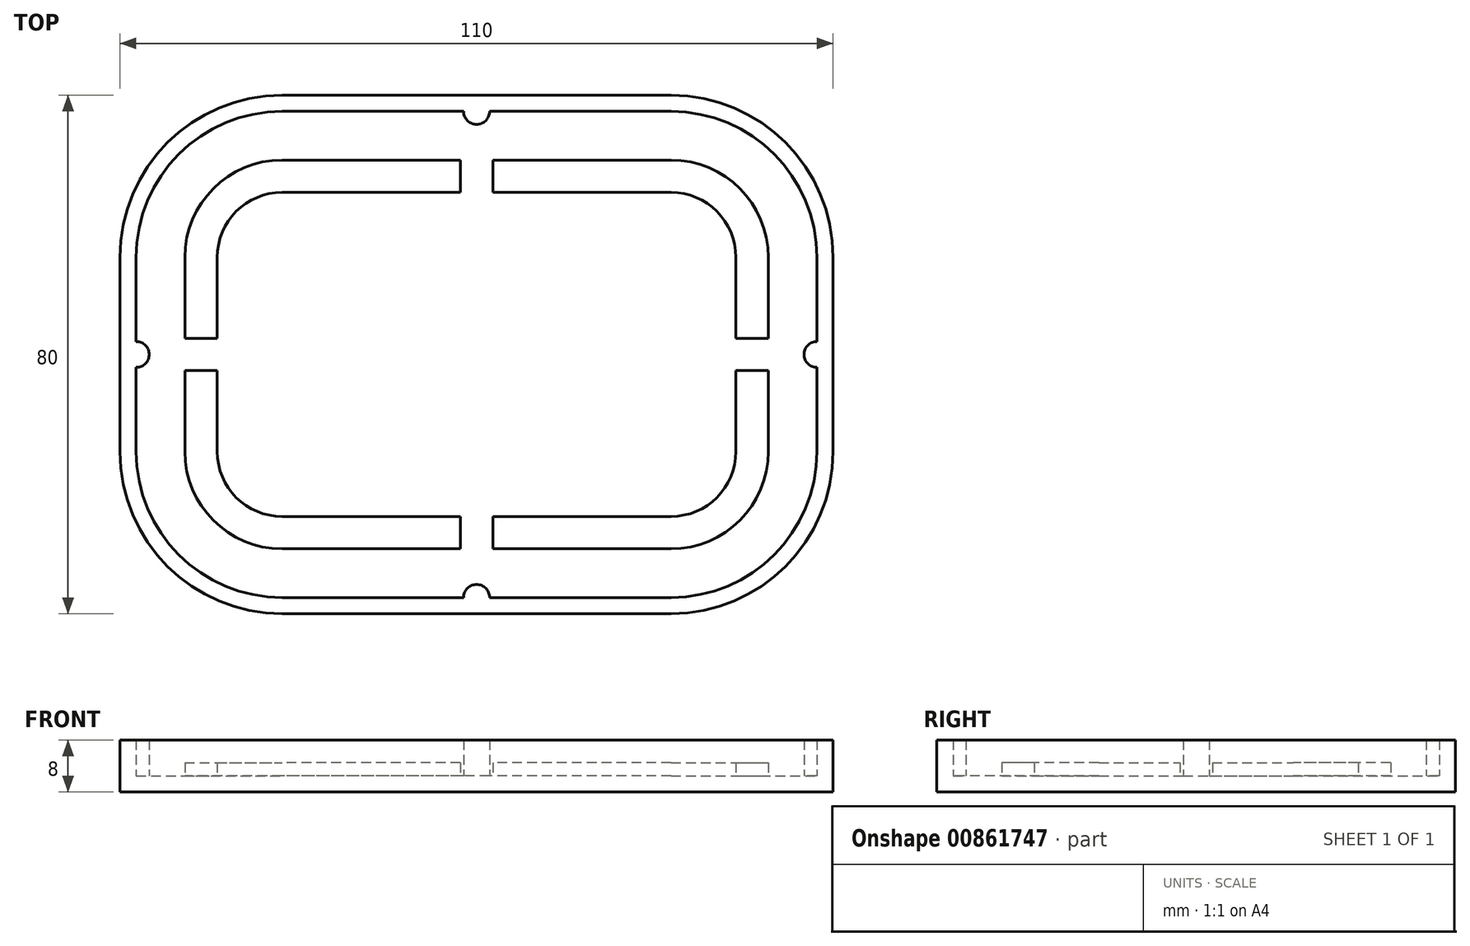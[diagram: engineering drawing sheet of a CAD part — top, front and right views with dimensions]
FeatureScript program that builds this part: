
annotation { "Feature Type Name" : "Feature", "Feature Type Description" : "" }
export const myFeature = defineFeature(function(context is Context, id is Id, definition is map)
    precondition{}
    {
        {
            var Q0;
            Q0=qCreatedBy(makeId("Top.planeOp"),FACE);
            var sketch = newSketch(context, id + "F0", { "sketchPlane" : qUnion([Q0])});
            skLineSegment(sketch, "E0.bottom", {"start": v(30, -40) * mm, "end": v(-30, -40) * mm});
            skLineSegment(sketch, "E0.top", {"start": v(30, 40) * mm, "end": v(-30, 40) * mm});
            skLineSegment(sketch, "E0.left", {"start": v(55, -15) * mm, "end": v(55, 15) * mm});
            skLineSegment(sketch, "E0.right", {"start": v(-55, -15) * mm, "end": v(-55, 15) * mm});
            skPoint(sketch, "E0.middle", {"position": v(0, 0) * mm});
            skPoint(sketch, "E1.visualSharp", {"position": v(-55, 40) * mm});
            skArc(sketch, "E1.filletArc", {"start": v(-30, 40) * mm, "mid": v(-47.68, 32.68) * mm, "end": v(-55, 15) * mm});
            skPoint(sketch, "E2.visualSharp", {"position": v(55, 40) * mm});
            skArc(sketch, "E2.filletArc", {"start": v(55, 15) * mm, "mid": v(47.68, 32.68) * mm, "end": v(30, 40) * mm});
            skPoint(sketch, "E3.visualSharp", {"position": v(55, -40) * mm});
            skArc(sketch, "E3.filletArc", {"start": v(30, -40) * mm, "mid": v(47.68, -32.68) * mm, "end": v(55, -15) * mm});
            skPoint(sketch, "E4.visualSharp", {"position": v(-55, -40) * mm});
            skArc(sketch, "E4.filletArc", {"start": v(-55, -15) * mm, "mid": v(-47.68, -32.68) * mm, "end": v(-30, -40) * mm});
            skSolve(sketch);
        }
        {
            var Q0;
            Q0=makeQuery(id+"F0.imprint","IMPRINT",FACE,{"disambiguationData":[TD([[makeQuery(id+"F0.imprint","IMPRINT",EDGE,{"derivedFrom":sQuery(id+"F0.wireOp",EDGE,"E0.bottom")}),-1.0]])]});
            extrude(context, id + "F1", {"entities" : qUnion([Q0]), "depth" : 8 * mm, "offsetDistance" : 25 * mm});
        }
        {
            var Q0;
            Q0=makeQuery(id+"F1.opExtrude","CAP_FACE",FACE,{"disambiguationData":[OSD([sQuery(id+"F0.wireOp",EDGE,"E0.bottom"),sQuery(id+"F0.wireOp",EDGE,"E0.top"),sQuery(id+"F0.wireOp",EDGE,"E0.left"),sQuery(id+"F0.wireOp",EDGE,"E0.right"),sQuery(id+"F0.wireOp",EDGE,"E1.filletArc"),sQuery(id+"F0.wireOp",EDGE,"E2.filletArc"),sQuery(id+"F0.wireOp",EDGE,"E3.filletArc"),sQuery(id+"F0.wireOp",EDGE,"E4.filletArc")])],"isStart":false});
            shell(context, id + "F2", {"entities" : qUnion([Q0]), "thickness" : 2.5 * mm});
        }
        {
            var Q0;
            Q0=makeQuery(id+"F2.opShell","OFFSET_FACE",FACE,{"disambiguationData":[OSD([sQuery(id+"F0.wireOp",EDGE,"E0.bottom"),sQuery(id+"F0.wireOp",EDGE,"E0.top"),sQuery(id+"F0.wireOp",EDGE,"E0.left"),sQuery(id+"F0.wireOp",EDGE,"E0.right"),sQuery(id+"F0.wireOp",EDGE,"E1.filletArc"),sQuery(id+"F0.wireOp",EDGE,"E2.filletArc"),sQuery(id+"F0.wireOp",EDGE,"E3.filletArc"),sQuery(id+"F0.wireOp",EDGE,"E4.filletArc")])]});
            var sketch = newSketch(context, id + "F3", { "sketchPlane" : qUnion([Q0])});
            skLineSegment(sketch, "E5.bottom", {"start": v(30, -30) * mm, "end": v(-30, -30) * mm});
            skLineSegment(sketch, "E5.top", {"start": v(30, 30) * mm, "end": v(-30, 30) * mm});
            skLineSegment(sketch, "E5.left", {"start": v(45, -15) * mm, "end": v(45, 15) * mm});
            skLineSegment(sketch, "E5.right", {"start": v(-45, -15) * mm, "end": v(-45, 15) * mm});
            skPoint(sketch, "E5.middle", {"position": v(0, 0) * mm});
            skPoint(sketch, "E6.visualSharp", {"position": v(-45, 30) * mm});
            skArc(sketch, "E6.filletArc", {"start": v(-30, 30) * mm, "mid": v(-40.6, 25.6) * mm, "end": v(-45, 15) * mm});
            skPoint(sketch, "E7.visualSharp", {"position": v(45, 30) * mm});
            skArc(sketch, "E7.filletArc", {"start": v(45, 15) * mm, "mid": v(40.6, 25.6) * mm, "end": v(30, 30) * mm});
            skPoint(sketch, "E8.visualSharp", {"position": v(45, -30) * mm});
            skArc(sketch, "E8.filletArc", {"start": v(30, -30) * mm, "mid": v(40.6, -25.6) * mm, "end": v(45, -15) * mm});
            skPoint(sketch, "E9.visualSharp", {"position": v(-45, -30) * mm});
            skArc(sketch, "E9.filletArc", {"start": v(-45, -15) * mm, "mid": v(-40.6, -25.6) * mm, "end": v(-30, -30) * mm});
            skArc(sketch, "E10.0", {"start": v(40, 15) * mm, "mid": v(37.07, 22.07) * mm, "end": v(30, 25) * mm});
            skLineSegment(sketch, "E10.1", {"start": v(40, -15) * mm, "end": v(40, 15) * mm});
            skLineSegment(sketch, "E10.2", {"start": v(30, 25) * mm, "end": v(-30, 25) * mm});
            skArc(sketch, "E10.3", {"start": v(30, -25) * mm, "mid": v(37.07, -22.07) * mm, "end": v(40, -15) * mm});
            skArc(sketch, "E10.4", {"start": v(-30, 25) * mm, "mid": v(-37.07, 22.07) * mm, "end": v(-40, 15) * mm});
            skLineSegment(sketch, "E10.5", {"start": v(-40, -15) * mm, "end": v(-40, 15) * mm});
            skArc(sketch, "E10.6", {"start": v(-40, -15) * mm, "mid": v(-37.07, -22.07) * mm, "end": v(-30, -25) * mm});
            skLineSegment(sketch, "E10.7", {"start": v(30, -25) * mm, "end": v(-30, -25) * mm});
            skLineSegment(sketch, "E11", {"start": v(-2.5, 30) * mm, "end": v(-2.5, -30) * mm});
            skLineSegment(sketch, "E12", {"start": v(2.5, -30) * mm, "end": v(2.5, 30) * mm});
            skLineSegment(sketch, "E13", {"start": v(-45, 2.5) * mm, "end": v(45, 2.5) * mm});
            skLineSegment(sketch, "E14", {"start": v(-45, -2.5) * mm, "end": v(45, -2.5) * mm});
            skSolve(sketch);
        }
        {
            var Q0;
            {var subQ4=sQuery(id+"F3.wireOp",EDGE,"E6.filletArc");Q0=makeQuery(id+"F3.imprint","IMPRINT",FACE,{"disambiguationData":[TD([[makeQuery(id+"F3.imprint","IMPRINT",EDGE,{"derivedFrom":subQ4}),1.0]])]});}
            var Q1;
            {var subQ1=sQuery(id+"F3.wireOp",EDGE,"E7.filletArc");Q1=makeQuery(id+"F3.imprint","IMPRINT",FACE,{"disambiguationData":[TD([[makeQuery(id+"F3.imprint","IMPRINT",EDGE,{"derivedFrom":subQ1}),1.0]])]});}
            var Q2;
            {var subQ4=sQuery(id+"F3.wireOp",EDGE,"E8.filletArc");Q2=makeQuery(id+"F3.imprint","IMPRINT",FACE,{"disambiguationData":[TD([[makeQuery(id+"F3.imprint","IMPRINT",EDGE,{"derivedFrom":subQ4}),1.0]])]});}
            var Q3;
            {var subQ11=sQuery(id+"F3.wireOp",EDGE,"E9.filletArc");Q3=makeQuery(id+"F3.imprint","IMPRINT",FACE,{"disambiguationData":[TD([[makeQuery(id+"F3.imprint","IMPRINT",EDGE,{"derivedFrom":subQ11}),1.0]])]});}
            extrude(context, id + "F4", {"entities" : qUnion([Q0, Q1, Q2, Q3]), "operationType" : NewBodyOperationType.ADD, "depth" : 2 * mm, "offsetDistance" : 25 * mm});
        }
        {
            var Q0;
            Q0=makeQuery(id+"F2.opShell","OFFSET_FACE",FACE,{"disambiguationData":[OSD([sQuery(id+"F0.wireOp",EDGE,"E0.bottom"),sQuery(id+"F0.wireOp",EDGE,"E0.top"),sQuery(id+"F0.wireOp",EDGE,"E0.left"),sQuery(id+"F0.wireOp",EDGE,"E0.right"),sQuery(id+"F0.wireOp",EDGE,"E1.filletArc"),sQuery(id+"F0.wireOp",EDGE,"E2.filletArc"),sQuery(id+"F0.wireOp",EDGE,"E3.filletArc"),sQuery(id+"F0.wireOp",EDGE,"E4.filletArc")])]});
            var sketch = newSketch(context, id + "F5", { "sketchPlane" : qUnion([Q0])});
            skLineSegment(sketch, "E15.0", {"start": v(30, 37.5) * mm, "end": v(-30, 37.5) * mm});
            skLineSegment(sketch, "E16.0", {"start": v(30, -37.5) * mm, "end": v(-30, -37.5) * mm});
            skLineSegment(sketch, "E17.0", {"start": v(52.5, -15) * mm, "end": v(52.5, 15) * mm});
            skLineSegment(sketch, "E18.0", {"start": v(-52.5, -15) * mm, "end": v(-52.5, 15) * mm});
            skCircle(sketch, "E19", {"center": v(0, 37.5) * mm, "radius": 2 * mm});
            skCircle(sketch, "E20", {"center": v(0, -37.5) * mm, "radius": 2 * mm});
            skCircle(sketch, "E21", {"center": v(-52.5, 0) * mm, "radius": 2 * mm});
            skCircle(sketch, "E22", {"center": v(52.5, 0) * mm, "radius": 2 * mm});
            skSolve(sketch);
        }
        {
            var Q0;
            {var subQ0=sQuery(id+"F5.wireOp",EDGE,"E19");var subQ1=sQuery(id+"F5.wireOp",EDGE,"E15.0");var subQ2=makeQuery(id+"F5.imprint","INTERSECT",VERTEX,{"disambiguationData":[OD(0.0)],"derivedFrom":[subQ1,subQ0]});Q0=makeQuery(id+"F5.imprint","IMPRINT",FACE,{"disambiguationData":[TD([[makeQuery(id+"F5.imprint","IMPRINT",EDGE,{"disambiguationData":[TD([[subQ2,-1.0]])],"derivedFrom":subQ1}),1.0]])]});}
            var Q1;
            {var subQ0=sQuery(id+"F5.wireOp",EDGE,"E22");var subQ1=sQuery(id+"F5.wireOp",EDGE,"E17.0");var subQ2=makeQuery(id+"F5.imprint","INTERSECT",VERTEX,{"disambiguationData":[OD(0.0)],"derivedFrom":[subQ1,subQ0]});Q1=makeQuery(id+"F5.imprint","IMPRINT",FACE,{"disambiguationData":[TD([[makeQuery(id+"F5.imprint","IMPRINT",EDGE,{"disambiguationData":[TD([[subQ2,-1.0]])],"derivedFrom":subQ1}),1.0]])]});}
            var Q2;
            {var subQ0=sQuery(id+"F5.wireOp",EDGE,"E20");var subQ1=sQuery(id+"F5.wireOp",EDGE,"E16.0");var subQ2=makeQuery(id+"F5.imprint","INTERSECT",VERTEX,{"disambiguationData":[OD(0.0)],"derivedFrom":[subQ1,subQ0]});Q2=makeQuery(id+"F5.imprint","IMPRINT",FACE,{"disambiguationData":[TD([[makeQuery(id+"F5.imprint","IMPRINT",EDGE,{"disambiguationData":[TD([[subQ2,-1.0]])],"derivedFrom":subQ1}),-1.0]])]});}
            var Q3;
            {var subQ0=sQuery(id+"F5.wireOp",EDGE,"E21");var subQ1=sQuery(id+"F5.wireOp",EDGE,"E18.0");var subQ2=makeQuery(id+"F5.imprint","INTERSECT",VERTEX,{"disambiguationData":[OD(0.0)],"derivedFrom":[subQ1,subQ0]});Q3=makeQuery(id+"F5.imprint","IMPRINT",FACE,{"disambiguationData":[TD([[makeQuery(id+"F5.imprint","IMPRINT",EDGE,{"disambiguationData":[TD([[subQ2,-1.0]])],"derivedFrom":subQ1}),-1.0]])]});}
            var Q4;
            Q4=makeQuery(id+"F1.opExtrude","CAP_FACE",FACE,{"disambiguationData":[OSD([sQuery(id+"F0.wireOp",EDGE,"E0.bottom"),sQuery(id+"F0.wireOp",EDGE,"E0.top"),sQuery(id+"F0.wireOp",EDGE,"E0.left"),sQuery(id+"F0.wireOp",EDGE,"E0.right"),sQuery(id+"F0.wireOp",EDGE,"E1.filletArc"),sQuery(id+"F0.wireOp",EDGE,"E2.filletArc"),sQuery(id+"F0.wireOp",EDGE,"E3.filletArc"),sQuery(id+"F0.wireOp",EDGE,"E4.filletArc")])],"isStart":false});
            extrude(context, id + "F6", {"entities" : qUnion([Q0, Q1, Q2, Q3]), "operationType" : NewBodyOperationType.ADD, "endBound" : BoundingType.UP_TO_SURFACE, "depth" : 25 * mm, "endBoundEntityFace" : qUnion([Q4]), "offsetDistance" : 25 * mm});
        }
    });
